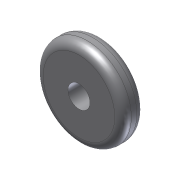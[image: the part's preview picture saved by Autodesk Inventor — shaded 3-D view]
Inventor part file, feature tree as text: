
AUTODESK INVENTOR PART (.ipt)
format: ipt  version: 2012 (Build 160160000, 160)  size: 118,272 bytes
history: native  units: in
note: dims shown in document units (in); Inventor stores cm internally (conversion verified against a paired STEP export)
features: extrude x2, sketch x2, fillet x1
ambient origin geometry x8: Origin, YZ Plane, XZ Plane, XY Plane, X Axis, Y Axis, Z Axis, Center Point
bodies: Solid1 (feature_tree)
feature tree (5):
  extrude  "Extrusion1"  Depth=2.0in TaperAngle=0.0deg
  fillet  "Fillet1"  Radius=0.75in
  extrude  "Extrusion2"  Depth=2.0in TaperAngle=0.0deg
  sketch  "Sketch1"  dims[d0=8.0in d1=2.0in d2=0.0in d3=0.75in]
  sketch  "Sketch2"  dims[d4=2.0in d5=2.0in d6=0.0in]
